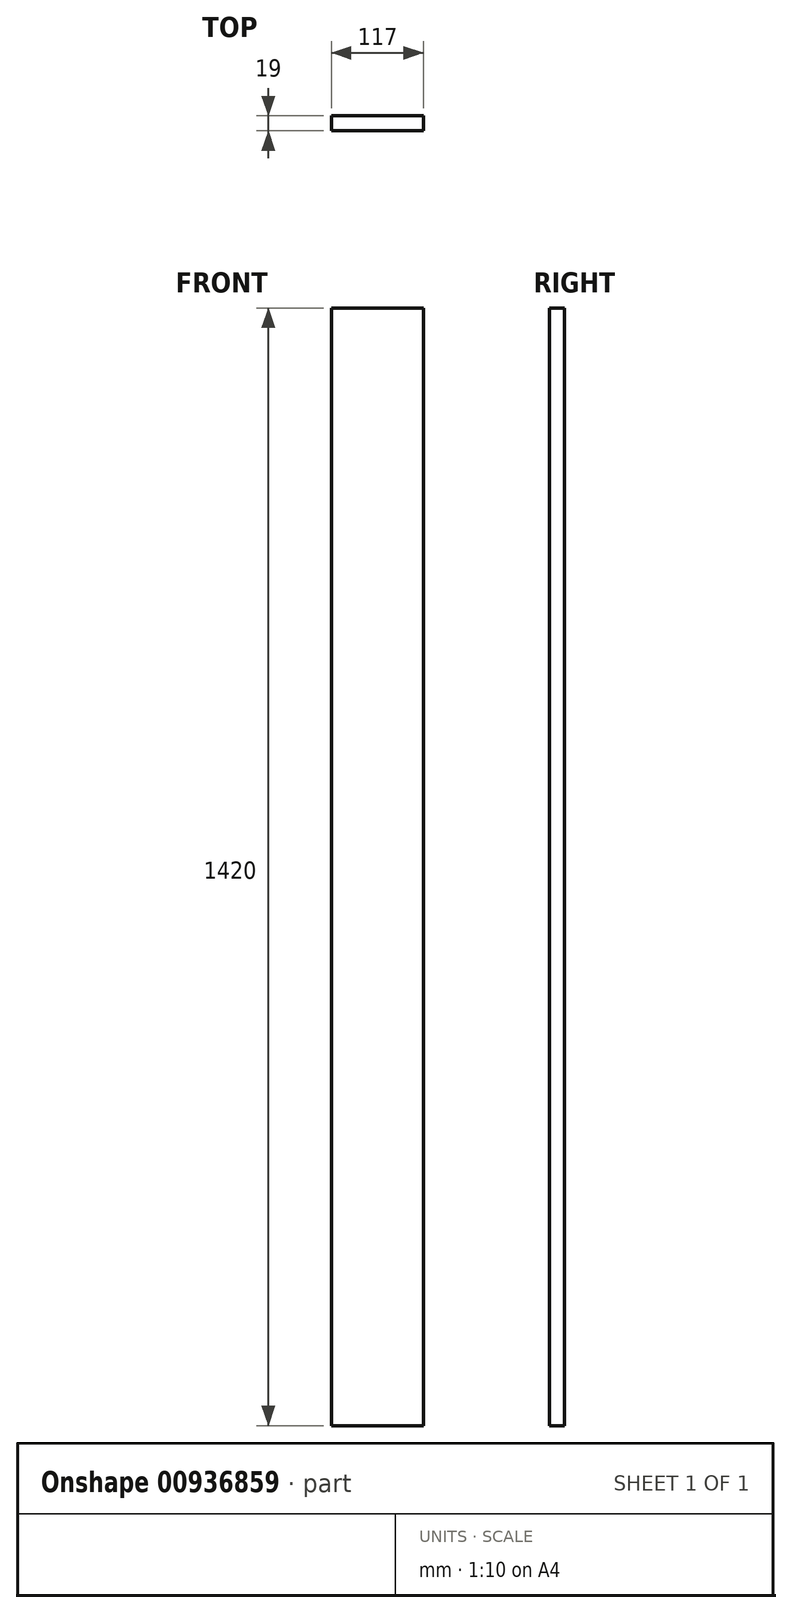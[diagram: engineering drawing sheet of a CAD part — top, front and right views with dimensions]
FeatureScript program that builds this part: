
annotation { "Feature Type Name" : "Feature", "Feature Type Description" : "" }
export const myFeature = defineFeature(function(context is Context, id is Id, definition is map)
    precondition{}
    {
        {
            var Q0;
            Q0=qCreatedBy(makeId("Top.planeOp"),FACE);
            var sketch = newSketch(context, id + "F0", { "sketchPlane" : qUnion([Q0])});
            skLineSegment(sketch, "E0.bottom", {"start": v(-58.5, -9.5) * mm, "end": v(58.5, -9.5) * mm});
            skLineSegment(sketch, "E0.top", {"start": v(-58.5, 9.5) * mm, "end": v(58.5, 9.5) * mm});
            skLineSegment(sketch, "E0.left", {"start": v(-58.5, -9.5) * mm, "end": v(-58.5, 9.5) * mm});
            skLineSegment(sketch, "E0.right", {"start": v(58.5, -9.5) * mm, "end": v(58.5, 9.5) * mm});
            skSolve(sketch);
        }
        {
            var Q0;
            Q0=makeQuery(id+"F0.imprint","IMPRINT",FACE,{"disambiguationData":[TD([[makeQuery(id+"F0.imprint","IMPRINT",EDGE,{"derivedFrom":sQuery(id+"F0.wireOp",EDGE,"E0.bottom")}),1.0]])]});
            extrude(context, id + "F1", {"entities" : qUnion([Q0]), "depth" : 1420 * mm, "offsetDistance" : 25 * mm});
        }
    });
